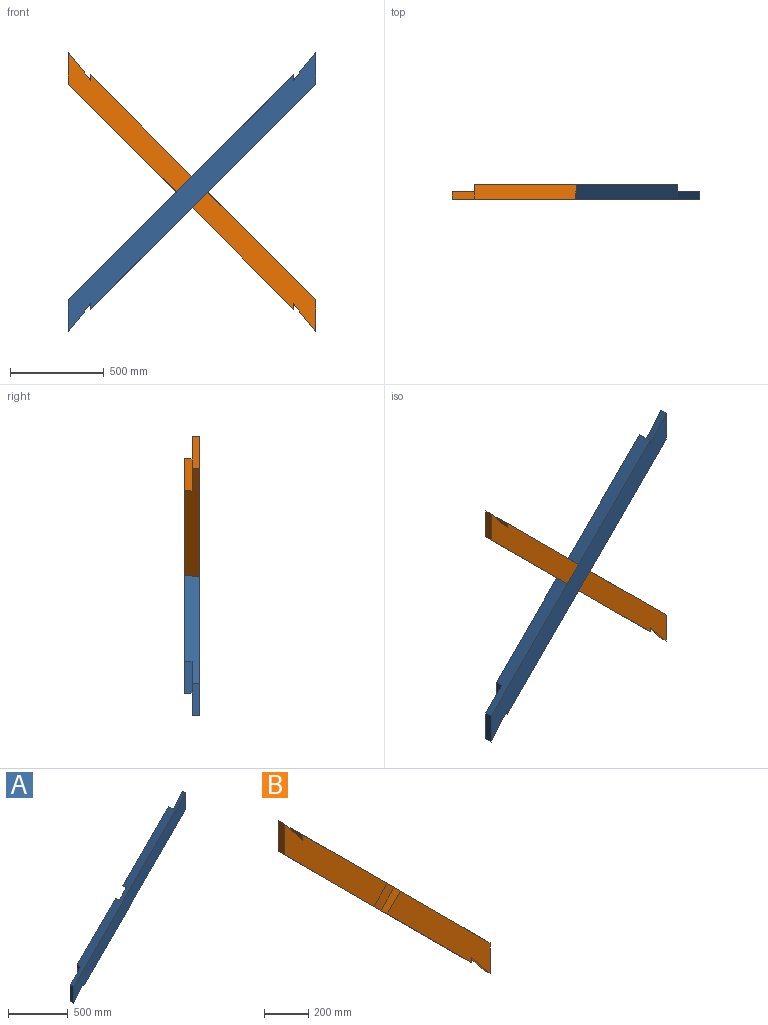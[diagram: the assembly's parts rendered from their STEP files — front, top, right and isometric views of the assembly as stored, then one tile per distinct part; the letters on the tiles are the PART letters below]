
ASSEMBLY  parts=2 mates=1
PART A: 16 faces, bbox 1320x80x1489.7 mm
  f0: plane 289.71x120mm, normal (0,1,0), area 18667.6mm2, adj f2,f3,f8,f9
  f1: plane 289.71x120mm, normal (0,1,0), area 18667.6mm2, adj f4,f5,f6,f7
  f2: plane 148.28x120mm, normal (-0.78,0,0.63), area 7630.3mm2, adj f0,f3,f9,f10
  f3: plane 169.71x80mm, normal (1,0,0), area 7919.6mm2, adj f0,f2,f4,f8,f10,f15
  f4: plane 1200x1200mm, normal (-0.71,0,0.71), area 124176.3mm2, adj f1,f3,f5,f7,f10,f11,f12,f13
  f5: plane 169.71x40mm, normal (-1,0,0), area 6788.2mm2, adj f1,f4,f6,f10
  f6: plane 148.28x120mm, normal (0.78,0,-0.63), area 7630.3mm2, adj f1,f5,f7,f10
  f7: plane 169.71x80mm, normal (-1,0,0), area 7919.6mm2, adj f1,f4,f6,f8,f10,f13
  f8: plane 1200x1200mm, normal (0.71,0,-0.71), area 124176.3mm2, adj f0,f3,f7,f9,f10,f11,f12,f13
  f9: plane 169.71x40mm, normal (1,0,0), area 6788.2mm2, adj f0,f2,f8,f10
  f10: plane 1489.71x1320mm, normal (0,-1,0), area 220617.3mm2, adj f2,f3,f4,f5,f6,f7,f8,f9
  f11: plane 169.71x169.71mm, normal (0,1,0), area 14400mm2, adj f4,f8,f12,f14
  f12: plane 84.85x84.85mm, normal (0.71,0,0.71), area 4800mm2, adj f4,f8,f11,f13
  f13: plane 624.85x540mm, normal (0,1,0), area 84441mm2, adj f4,f7,f8,f12
  f14: plane 84.85x84.85mm, normal (-0.71,0,-0.71), area 4800mm2, adj f4,f8,f11,f15
  f15: plane 624.85x540mm, normal (0,1,0), area 84441mm2, adj f3,f4,f8,f14
PART B: 16 faces, bbox 1320x80x1489.7 mm
  f0: plane 289.71x120mm, normal (0,1,0), area 18667.6mm2, adj f1,f2,f5,f6
  f1: plane 169.71x40mm, normal (-1,0,0), area 6788.2mm2, adj f0,f2,f6,f7
  f2: plane 1200x1200mm, normal (-0.71,0,-0.71), area 124176.3mm2, adj f0,f1,f3,f5,f7,f8,f11,f12
  f3: plane 84.85x84.85mm, normal (0.71,0,-0.71), area 4800mm2, adj f2,f4,f7,f15
  f4: plane 1200x1200mm, normal (0.71,0,0.71), area 124176.3mm2, adj f3,f5,f7,f8,f10,f11,f12,f13
  f5: plane 169.71x80mm, normal (-1,0,0), area 7919.6mm2, adj f0,f2,f4,f6,f7,f14
  f6: plane 148.28x120mm, normal (0.78,0,0.63), area 7630.3mm2, adj f0,f1,f5,f7
  f7: plane 744.85x660mm, normal (0,-1,0), area 103108.7mm2, adj f1,f2,f3,f4,f5,f6
  f8: plane 169.71x80mm, normal (1,0,0), area 7919.6mm2, adj f2,f4,f9,f12,f13,f14
  f9: plane 148.28x120mm, normal (-0.78,0,-0.63), area 7630.3mm2, adj f8,f10,f12,f13
  f10: plane 169.71x40mm, normal (1,0,0), area 6788.2mm2, adj f4,f9,f12,f13
  f11: plane 84.85x84.85mm, normal (-0.71,0,0.71), area 4800mm2, adj f2,f4,f12,f15
  f12: plane 744.85x660mm, normal (0,-1,0), area 103108.7mm2, adj f2,f4,f8,f9,f10,f11
  f13: plane 289.71x120mm, normal (0,1,0), area 18667.6mm2, adj f4,f8,f9,f10
  f14: plane 1249.71x1080mm, normal (0,1,0), area 183282.1mm2, adj f2,f4,f5,f8
  f15: plane 169.71x169.71mm, normal (0,-1,0), area 14400mm2, adj f2,f3,f4,f11
PLACE A t=(-403.81,228.17,-314.61)mm
PLACE B t=(-403.81,228.17,-314.61)mm
MATE fastened B.f15 <-> A.f11  axis (0,-1,0) through (-403.81,228.17,691.97)mm
